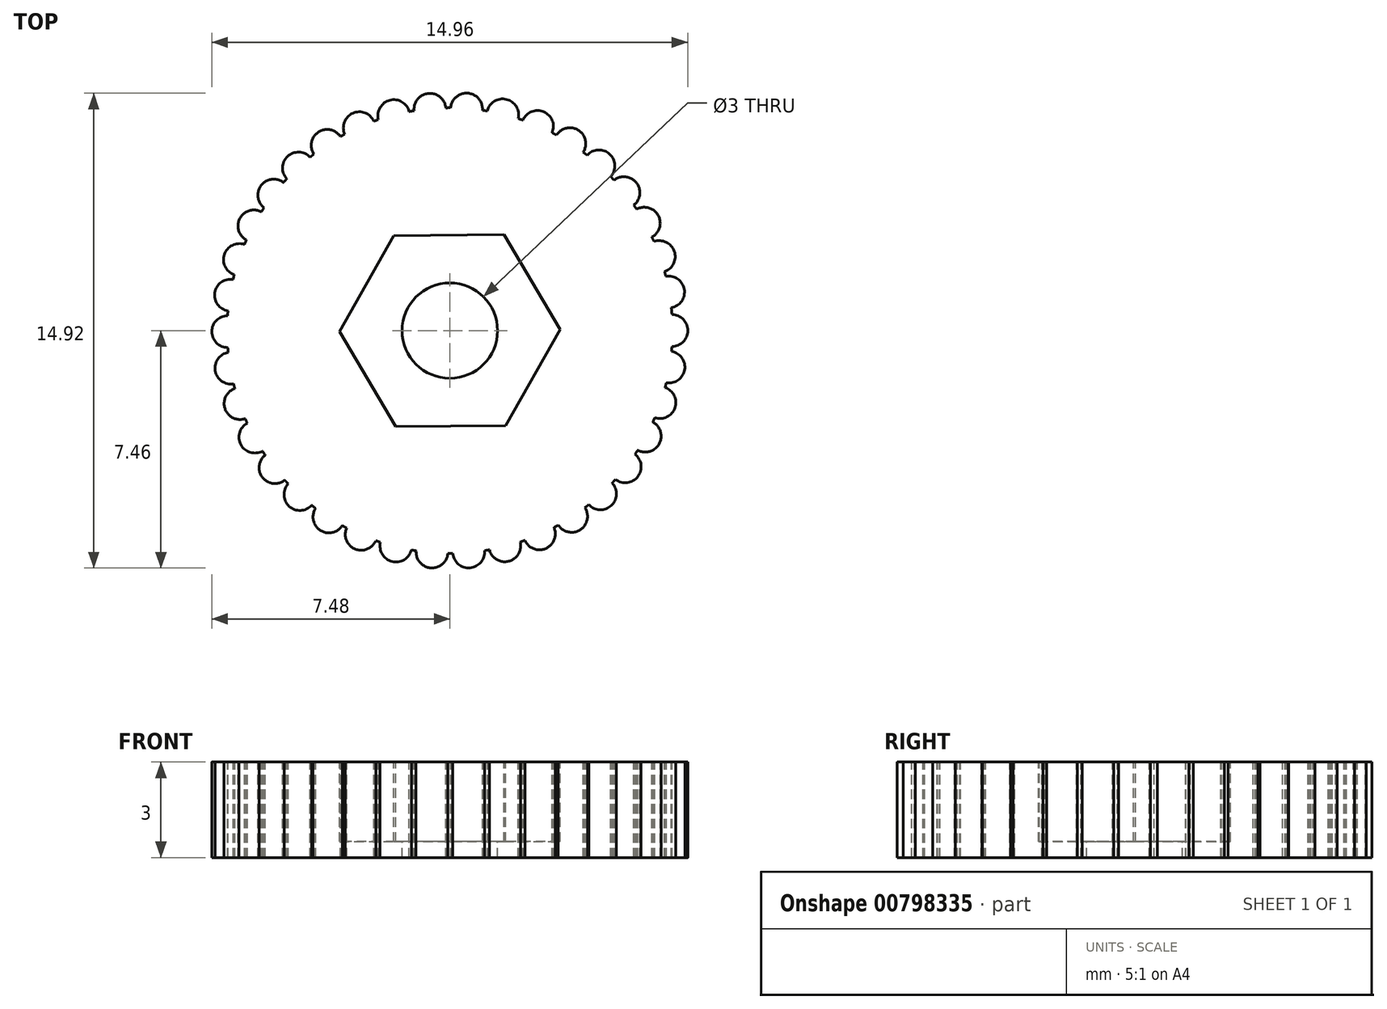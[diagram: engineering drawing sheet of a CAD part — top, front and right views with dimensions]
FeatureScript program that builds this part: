
annotation { "Feature Type Name" : "Feature", "Feature Type Description" : "" }
export const myFeature = defineFeature(function(context is Context, id is Id, definition is map)
    precondition{}
    {
        {
            var Q0;
            Q0=qCreatedBy(makeId("Top.planeOp"),FACE);
            var sketch = newSketch(context, id + "F0", { "sketchPlane" : qUnion([Q0])});
            skCircle(sketch, "E0", {"center": v(0, 0) * mm, "radius": 7 * mm});
            skCircle(sketch, "E1.cCircle", {"center": v(0, 0) * mm, "radius": 3 * mm, "construction": true});
            skLineSegment(sketch, "E1.0", {"start": v(3.46, 0.03) * mm, "end": v(1.76, -2.98) * mm});
            skLineSegment(sketch, "E1.1", {"start": v(1.76, -2.98) * mm, "end": v(-1.7, -3.02) * mm});
            skLineSegment(sketch, "E1.2", {"start": v(-1.7, -3.02) * mm, "end": v(-3.46, -0.03) * mm});
            skLineSegment(sketch, "E1.3", {"start": v(-3.46, -0.03) * mm, "end": v(-1.76, 2.98) * mm});
            skLineSegment(sketch, "E1.4", {"start": v(-1.76, 2.98) * mm, "end": v(1.7, 3.02) * mm});
            skLineSegment(sketch, "E1.5", {"start": v(1.7, 3.02) * mm, "end": v(3.46, 0.03) * mm});
            skPoint(sketch, "E1.0.midPoint", {"position": v(2.61, -1.48) * mm});
            skCircle(sketch, "E2", {"center": v(0, 0) * mm, "radius": 1.5 * mm});
            skLineSegment(sketch, "E3", {"start": v(6.4, 0) * mm, "end": v(8.22, 0) * mm, "construction": true});
            skArc(sketch, "E4", {"start": v(6.98, -0.5) * mm, "mid": v(7.48, 0) * mm, "end": v(6.98, 0.5) * mm});
            skArc(sketch, "E5.1.0", {"start": v(6.8, -1.64) * mm, "mid": v(7.38, -1.23) * mm, "end": v(6.97, -0.65) * mm});
            skArc(sketch, "E5.2.0", {"start": v(6.44, -2.74) * mm, "mid": v(7.08, -2.43) * mm, "end": v(6.77, -1.8) * mm});
            skArc(sketch, "E5.3.0", {"start": v(5.9, -3.76) * mm, "mid": v(6.58, -3.56) * mm, "end": v(6.38, -2.88) * mm});
            skArc(sketch, "E5.4.0", {"start": v(5.2, -4.68) * mm, "mid": v(5.9, -4.59) * mm, "end": v(5.82, -3.89) * mm});
            skArc(sketch, "E5.5.0", {"start": v(4.37, -5.47) * mm, "mid": v(5.07, -5.5) * mm, "end": v(5.1, -4.8) * mm});
            skArc(sketch, "E5.6.0", {"start": v(3.4, -6.11) * mm, "mid": v(4.1, -6.26) * mm, "end": v(4.25, -5.57) * mm});
            skArc(sketch, "E5.7.0", {"start": v(2.36, -6.6) * mm, "mid": v(3.02, -6.85) * mm, "end": v(3.27, -6.19) * mm});
            skArc(sketch, "E5.8.0", {"start": v(1.24, -6.89) * mm, "mid": v(1.85, -7.25) * mm, "end": v(2.21, -6.64) * mm});
            skArc(sketch, "E5.9.0", {"start": v(0.1, -7) * mm, "mid": v(0.63, -7.46) * mm, "end": v(1.1, -6.91) * mm});
            skArc(sketch, "E5.10.0", {"start": v(-1.06, -6.92) * mm, "mid": v(-0.6, -7.46) * mm, "end": v(-0.06, -7) * mm});
            skArc(sketch, "E5.11.0", {"start": v(-2.18, -6.65) * mm, "mid": v(-1.82, -7.26) * mm, "end": v(-1.21, -6.9) * mm});
            skArc(sketch, "E5.12.0", {"start": v(-3.24, -6.2) * mm, "mid": v(-2.99, -6.86) * mm, "end": v(-2.33, -6.6) * mm});
            skArc(sketch, "E5.13.0", {"start": v(-4.22, -5.59) * mm, "mid": v(-4.07, -6.28) * mm, "end": v(-3.38, -6.13) * mm});
            skArc(sketch, "E5.14.0", {"start": v(-5.08, -4.82) * mm, "mid": v(-5.05, -5.52) * mm, "end": v(-4.34, -5.5) * mm});
            skArc(sketch, "E5.15.0", {"start": v(-5.8, -3.92) * mm, "mid": v(-5.89, -4.62) * mm, "end": v(-5.19, -4.7) * mm});
            skArc(sketch, "E5.16.0", {"start": v(-6.37, -2.9) * mm, "mid": v(-6.57, -3.59) * mm, "end": v(-5.89, -3.79) * mm});
            skArc(sketch, "E5.17.0", {"start": v(-6.76, -1.82) * mm, "mid": v(-7.07, -2.46) * mm, "end": v(-6.43, -2.77) * mm});
            skArc(sketch, "E5.18.0", {"start": v(-6.97, -0.69) * mm, "mid": v(-7.37, -1.26) * mm, "end": v(-6.8, -1.67) * mm});
            skArc(sketch, "E5.19.0", {"start": v(-6.98, 0.47) * mm, "mid": v(-7.48, -0.04) * mm, "end": v(-6.98, -0.53) * mm});
            skArc(sketch, "E5.20.0", {"start": v(-6.81, 1.6) * mm, "mid": v(-7.39, 1.2) * mm, "end": v(-6.97, 0.62) * mm});
            skArc(sketch, "E5.21.0", {"start": v(-6.46, 2.7) * mm, "mid": v(-7.09, 2.4) * mm, "end": v(-6.78, 1.76) * mm});
            skArc(sketch, "E5.22.0", {"start": v(-5.92, 3.73) * mm, "mid": v(-6.6, 3.53) * mm, "end": v(-6.4, 2.85) * mm});
            skArc(sketch, "E5.23.0", {"start": v(-5.23, 4.65) * mm, "mid": v(-5.93, 4.56) * mm, "end": v(-5.84, 3.86) * mm});
            skArc(sketch, "E5.24.0", {"start": v(-4.4, 5.45) * mm, "mid": v(-5.1, 5.47) * mm, "end": v(-5.13, 4.77) * mm});
            skArc(sketch, "E5.25.0", {"start": v(-3.44, 6.1) * mm, "mid": v(-4.13, 6.24) * mm, "end": v(-4.27, 5.55) * mm});
            skArc(sketch, "E5.26.0", {"start": v(-2.39, 6.58) * mm, "mid": v(-3.05, 6.83) * mm, "end": v(-3.3, 6.17) * mm});
            skArc(sketch, "E5.27.0", {"start": v(-1.28, 6.88) * mm, "mid": v(-1.89, 7.24) * mm, "end": v(-2.24, 6.63) * mm});
            skArc(sketch, "E5.28.0", {"start": v(-0.13, 7) * mm, "mid": v(-0.67, 7.45) * mm, "end": v(-1.12, 6.9) * mm});
            skArc(sketch, "E5.29.0", {"start": v(1.03, 6.92) * mm, "mid": v(0.56, 7.46) * mm, "end": v(0.03, 7) * mm});
            skArc(sketch, "E5.30.0", {"start": v(2.15, 6.66) * mm, "mid": v(1.78, 7.27) * mm, "end": v(1.18, 6.9) * mm});
            skArc(sketch, "E5.31.0", {"start": v(3.21, 6.22) * mm, "mid": v(2.95, 6.87) * mm, "end": v(2.3, 6.61) * mm});
            skArc(sketch, "E5.32.0", {"start": v(4.2, 5.6) * mm, "mid": v(4.04, 6.3) * mm, "end": v(3.35, 6.15) * mm});
            skArc(sketch, "E5.33.0", {"start": v(5.06, 4.84) * mm, "mid": v(5.02, 5.55) * mm, "end": v(4.32, 5.51) * mm});
            skArc(sketch, "E5.34.0", {"start": v(5.78, 3.94) * mm, "mid": v(5.87, 4.65) * mm, "end": v(5.16, 4.73) * mm});
            skLineSegment(sketch, "E5.anchor1", {"start": v(0, 0) * mm, "end": v(6.98, -0.5) * mm, "construction": true});
            skLineSegment(sketch, "E5.anchor2", {"start": v(0, 0) * mm, "end": v(6.96, 0.72) * mm, "construction": true});
            skArc(sketch, "E6.2.35.0", {"start": v(6.35, 2.94) * mm, "mid": v(6.55, 3.62) * mm, "end": v(5.87, 3.81) * mm});
            skArc(sketch, "E7.2.36.0", {"start": v(6.75, 1.85) * mm, "mid": v(7.05, 2.5) * mm, "end": v(6.42, 2.8) * mm});
            skArc(sketch, "E7.2.37.0", {"start": v(6.96, 0.72) * mm, "mid": v(7.37, 1.3) * mm, "end": v(6.79, 1.7) * mm});
            skSolve(sketch);
        }
        {
            var Q0;
            Q0=qSketchRegion(id+"F0",true);
            var Q1;
            Q1=makeQuery(id+"F0.imprint","IMPRINT",FACE,{"disambiguationData":[TD([[makeQuery(id+"F0.imprint","IMPRINT",EDGE,{"derivedFrom":sQuery(id+"F0.wireOp",EDGE,"E1.0")}),-1.0]])]});
            extrude(context, id + "F1", {"entities" : qUnion([Q0, Q1]), "flatOperationType" : FlatOperationType.REMOVE, "depth" : 3 * mm, "offsetDistance" : 25 * mm, "domain" : OperationDomain.MODEL});
        }
        {
            var Q0;
            Q0=makeQuery(id+"F0.imprint","IMPRINT",FACE,{"disambiguationData":[TD([[makeQuery(id+"F0.imprint","IMPRINT",EDGE,{"derivedFrom":sQuery(id+"F0.wireOp",EDGE,"E1.0")}),-1.0]])]});
            extrude(context, id + "F2", {"entities" : qUnion([Q0]), "operationType" : NewBodyOperationType.REMOVE, "depth" : 2.5 * mm, "offsetDistance" : 25 * mm});
        }
        {
            var Q0;
            Q0=makeQuery(id+"F1.opExtrude","SWEPT_BODY",BODY,{"disambiguationData":[OSD([sQuery(id+"F0.wireOp",EDGE,"E0"),sQuery(id+"F0.wireOp",EDGE,"E2"),sQuery(id+"F0.wireOp",EDGE,"E4"),sQuery(id+"F0.wireOp",EDGE,"E5.1.0"),sQuery(id+"F0.wireOp",EDGE,"E5.2.0"),sQuery(id+"F0.wireOp",EDGE,"E5.3.0"),sQuery(id+"F0.wireOp",EDGE,"E5.4.0"),sQuery(id+"F0.wireOp",EDGE,"E5.5.0"),sQuery(id+"F0.wireOp",EDGE,"E5.6.0"),sQuery(id+"F0.wireOp",EDGE,"E5.7.0"),sQuery(id+"F0.wireOp",EDGE,"E5.8.0"),sQuery(id+"F0.wireOp",EDGE,"E5.9.0"),sQuery(id+"F0.wireOp",EDGE,"E5.10.0"),sQuery(id+"F0.wireOp",EDGE,"E5.11.0"),sQuery(id+"F0.wireOp",EDGE,"E5.12.0"),sQuery(id+"F0.wireOp",EDGE,"E5.13.0"),sQuery(id+"F0.wireOp",EDGE,"E5.14.0"),sQuery(id+"F0.wireOp",EDGE,"E5.15.0"),sQuery(id+"F0.wireOp",EDGE,"E5.16.0"),sQuery(id+"F0.wireOp",EDGE,"E5.17.0"),sQuery(id+"F0.wireOp",EDGE,"E5.18.0"),sQuery(id+"F0.wireOp",EDGE,"E5.19.0"),sQuery(id+"F0.wireOp",EDGE,"E5.20.0"),sQuery(id+"F0.wireOp",EDGE,"E5.21.0"),sQuery(id+"F0.wireOp",EDGE,"E5.22.0"),sQuery(id+"F0.wireOp",EDGE,"E5.23.0"),sQuery(id+"F0.wireOp",EDGE,"E5.24.0"),sQuery(id+"F0.wireOp",EDGE,"E5.25.0"),sQuery(id+"F0.wireOp",EDGE,"E5.26.0"),sQuery(id+"F0.wireOp",EDGE,"E5.27.0"),sQuery(id+"F0.wireOp",EDGE,"E5.28.0"),sQuery(id+"F0.wireOp",EDGE,"E5.29.0"),sQuery(id+"F0.wireOp",EDGE,"E5.30.0"),sQuery(id+"F0.wireOp",EDGE,"E5.31.0"),sQuery(id+"F0.wireOp",EDGE,"E5.32.0"),sQuery(id+"F0.wireOp",EDGE,"E5.33.0"),sQuery(id+"F0.wireOp",EDGE,"E5.34.0"),sQuery(id+"F0.wireOp",EDGE,"E6.2.35.0"),sQuery(id+"F0.wireOp",EDGE,"E7.2.36.0"),sQuery(id+"F0.wireOp",EDGE,"E7.2.37.0")])]});
            var Q1;
            Q1=qCreatedBy(makeId("Top.planeOp"),FACE);
            mirror(context, id + "F3", {"entities" : qUnion([Q0]), "mirrorPlane" : qUnion([Q1])});
        }
        {
            var Q0;
            Q0=makeQuery(id+"F1.opExtrude","SWEPT_BODY",BODY,{"disambiguationData":[OSD([sQuery(id+"F0.wireOp",EDGE,"E0"),sQuery(id+"F0.wireOp",EDGE,"E2"),sQuery(id+"F0.wireOp",EDGE,"E4"),sQuery(id+"F0.wireOp",EDGE,"E5.1.0"),sQuery(id+"F0.wireOp",EDGE,"E5.2.0"),sQuery(id+"F0.wireOp",EDGE,"E5.3.0"),sQuery(id+"F0.wireOp",EDGE,"E5.4.0"),sQuery(id+"F0.wireOp",EDGE,"E5.5.0"),sQuery(id+"F0.wireOp",EDGE,"E5.6.0"),sQuery(id+"F0.wireOp",EDGE,"E5.7.0"),sQuery(id+"F0.wireOp",EDGE,"E5.8.0"),sQuery(id+"F0.wireOp",EDGE,"E5.9.0"),sQuery(id+"F0.wireOp",EDGE,"E5.10.0"),sQuery(id+"F0.wireOp",EDGE,"E5.11.0"),sQuery(id+"F0.wireOp",EDGE,"E5.12.0"),sQuery(id+"F0.wireOp",EDGE,"E5.13.0"),sQuery(id+"F0.wireOp",EDGE,"E5.14.0"),sQuery(id+"F0.wireOp",EDGE,"E5.15.0"),sQuery(id+"F0.wireOp",EDGE,"E5.16.0"),sQuery(id+"F0.wireOp",EDGE,"E5.17.0"),sQuery(id+"F0.wireOp",EDGE,"E5.18.0"),sQuery(id+"F0.wireOp",EDGE,"E5.19.0"),sQuery(id+"F0.wireOp",EDGE,"E5.20.0"),sQuery(id+"F0.wireOp",EDGE,"E5.21.0"),sQuery(id+"F0.wireOp",EDGE,"E5.22.0"),sQuery(id+"F0.wireOp",EDGE,"E5.23.0"),sQuery(id+"F0.wireOp",EDGE,"E5.24.0"),sQuery(id+"F0.wireOp",EDGE,"E5.25.0"),sQuery(id+"F0.wireOp",EDGE,"E5.26.0"),sQuery(id+"F0.wireOp",EDGE,"E5.27.0"),sQuery(id+"F0.wireOp",EDGE,"E5.28.0"),sQuery(id+"F0.wireOp",EDGE,"E5.29.0"),sQuery(id+"F0.wireOp",EDGE,"E5.30.0"),sQuery(id+"F0.wireOp",EDGE,"E5.31.0"),sQuery(id+"F0.wireOp",EDGE,"E5.32.0"),sQuery(id+"F0.wireOp",EDGE,"E5.33.0"),sQuery(id+"F0.wireOp",EDGE,"E5.34.0"),sQuery(id+"F0.wireOp",EDGE,"E6.2.35.0"),sQuery(id+"F0.wireOp",EDGE,"E7.2.36.0"),sQuery(id+"F0.wireOp",EDGE,"E7.2.37.0")])]});
            deleteBodies(context, id + "F4", {"entities" : qUnion([Q0])});
        }
    });
